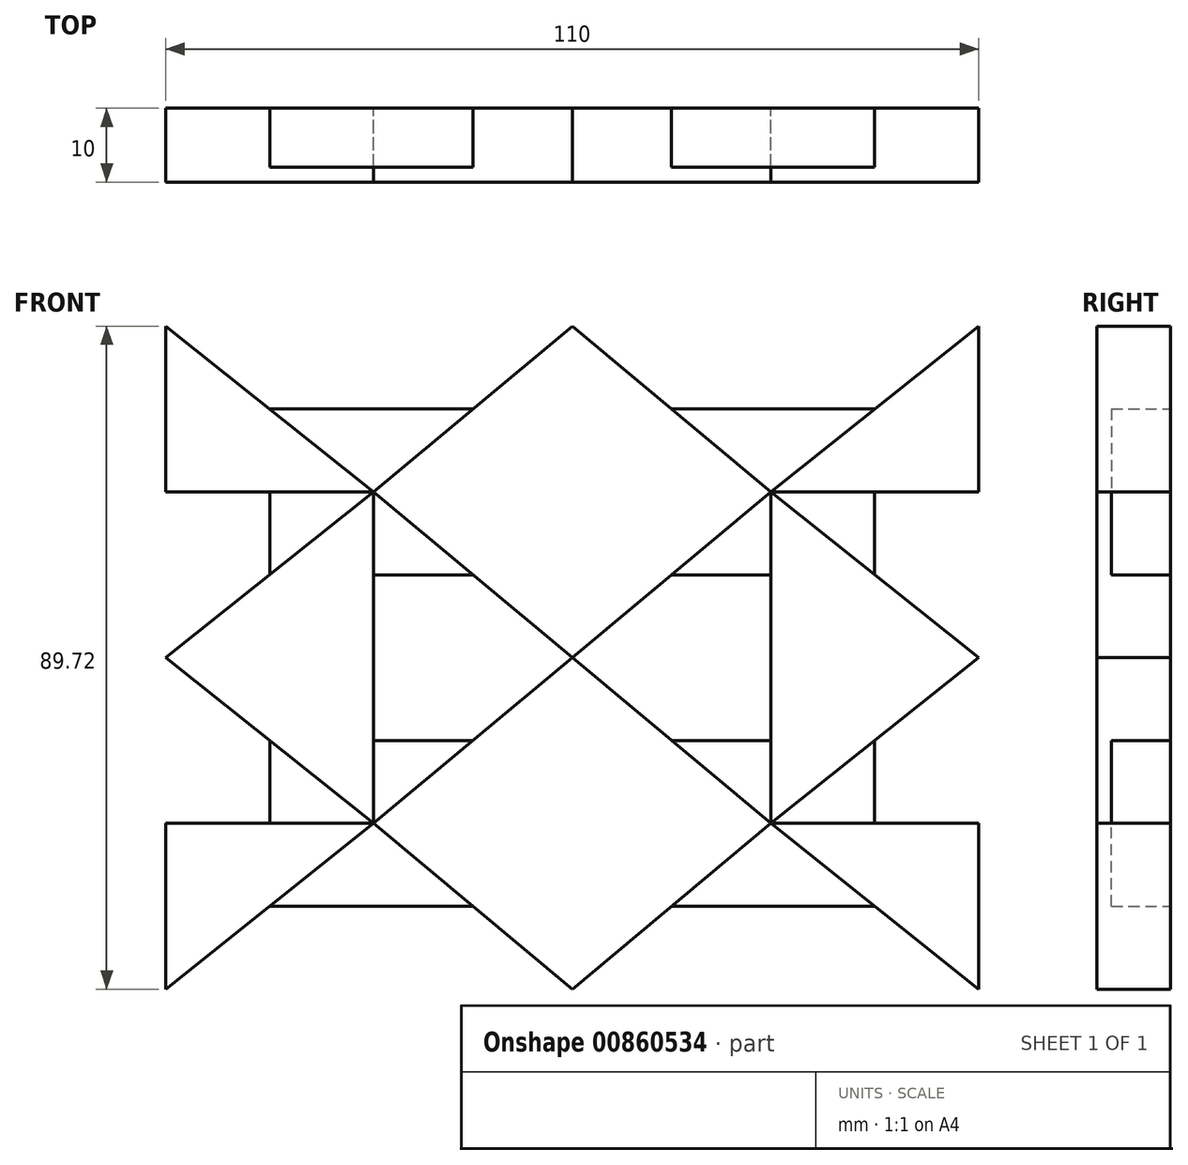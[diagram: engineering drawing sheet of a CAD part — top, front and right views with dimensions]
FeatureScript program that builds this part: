
annotation { "Feature Type Name" : "Feature", "Feature Type Description" : "" }
export const myFeature = defineFeature(function(context is Context, id is Id, definition is map)
    precondition{}
    {
        {
            var Q0;
            Q0=qCreatedBy(makeId("Front.planeOp"),FACE);
            var sketch = newSketch(context, id + "F0", { "sketchPlane" : qUnion([Q0])});
            skLineSegment(sketch, "E0", {"start": v(0, 0) * mm, "end": v(-26.87, 22.43) * mm});
            skLineSegment(sketch, "E1", {"start": v(-26.87, 22.43) * mm, "end": v(-55, 0) * mm});
            skLineSegment(sketch, "E2", {"start": v(0, 0) * mm, "end": v(26.87, 22.43) * mm});
            skLineSegment(sketch, "E3", {"start": v(26.87, 22.43) * mm, "end": v(55, 0) * mm});
            skLineSegment(sketch, "E4", {"start": v(0, 0) * mm, "end": v(-55, 0) * mm});
            skLineSegment(sketch, "E5", {"start": v(0, 0) * mm, "end": v(55, 0) * mm});
            skLineSegment(sketch, "E6", {"start": v(-26.87, 22.43) * mm, "end": v(-26.87, 0) * mm});
            skLineSegment(sketch, "E7", {"start": v(26.87, 22.43) * mm, "end": v(26.87, 0) * mm});
            skLineSegment(sketch, "E8", {"start": v(-26.87, 0) * mm, "end": v(-26.87, -22.43) * mm});
            skLineSegment(sketch, "E9", {"start": v(-55, 0) * mm, "end": v(-26.87, -22.43) * mm});
            skLineSegment(sketch, "E10", {"start": v(-26.87, -22.43) * mm, "end": v(0, 0) * mm});
            skLineSegment(sketch, "E11", {"start": v(26.87, 0) * mm, "end": v(26.87, -22.43) * mm});
            skLineSegment(sketch, "E12", {"start": v(0, 0) * mm, "end": v(26.87, -22.43) * mm});
            skLineSegment(sketch, "E13", {"start": v(26.87, -22.43) * mm, "end": v(55, 0) * mm});
            skLineSegment(sketch, "E14", {"start": v(0, 0) * mm, "end": v(0, 44.86) * mm});
            skLineSegment(sketch, "E15", {"start": v(0, 44.86) * mm, "end": v(-26.87, 22.43) * mm});
            skLineSegment(sketch, "E16", {"start": v(0, 44.86) * mm, "end": v(26.87, 22.43) * mm});
            skLineSegment(sketch, "E17", {"start": v(-55, 0) * mm, "end": v(-55, 22.43) * mm});
            skLineSegment(sketch, "E18", {"start": v(-55, 22.43) * mm, "end": v(-26.87, 22.43) * mm});
            skLineSegment(sketch, "E19", {"start": v(-55, 22.43) * mm, "end": v(-55, 44.86) * mm});
            skLineSegment(sketch, "E20", {"start": v(-55, 44.86) * mm, "end": v(0, 44.86) * mm});
            skLineSegment(sketch, "E21", {"start": v(-55, 44.86) * mm, "end": v(-26.87, 22.43) * mm});
            skLineSegment(sketch, "E22", {"start": v(55, 0) * mm, "end": v(55, 22.43) * mm});
            skLineSegment(sketch, "E23", {"start": v(55, 22.43) * mm, "end": v(26.87, 22.43) * mm});
            skLineSegment(sketch, "E24", {"start": v(55, 22.43) * mm, "end": v(55, 44.86) * mm});
            skLineSegment(sketch, "E25", {"start": v(55, 44.86) * mm, "end": v(0, 44.86) * mm});
            skLineSegment(sketch, "E26", {"start": v(0, 0) * mm, "end": v(0, -44.86) * mm});
            skLineSegment(sketch, "E27", {"start": v(0, -44.86) * mm, "end": v(-26.87, -22.43) * mm});
            skLineSegment(sketch, "E28", {"start": v(0, -44.86) * mm, "end": v(26.87, -22.43) * mm});
            skLineSegment(sketch, "E29", {"start": v(-55, 0) * mm, "end": v(-55, -22.43) * mm});
            skLineSegment(sketch, "E30", {"start": v(-55, -22.43) * mm, "end": v(-26.87, -22.43) * mm});
            skLineSegment(sketch, "E31", {"start": v(-55, -22.43) * mm, "end": v(-55, -44.86) * mm});
            skLineSegment(sketch, "E32", {"start": v(-55, -44.86) * mm, "end": v(0, -44.86) * mm});
            skLineSegment(sketch, "E33", {"start": v(-26.87, -22.43) * mm, "end": v(-55, -44.86) * mm});
            skLineSegment(sketch, "E34", {"start": v(0, -44.86) * mm, "end": v(55, -44.86) * mm});
            skLineSegment(sketch, "E35", {"start": v(55, 0) * mm, "end": v(55, -22.43) * mm});
            skLineSegment(sketch, "E36", {"start": v(55, -22.43) * mm, "end": v(26.87, -22.43) * mm});
            skLineSegment(sketch, "E37", {"start": v(55, -22.43) * mm, "end": v(55, -44.86) * mm});
            skLineSegment(sketch, "E38", {"start": v(26.87, -22.43) * mm, "end": v(55, -44.86) * mm});
            skLineSegment(sketch, "E39", {"start": v(26.87, 22.43) * mm, "end": v(55, 44.86) * mm});
            skLineSegment(sketch, "E40", {"start": v(-26.87, -11.21) * mm, "end": v(-13.44, -11.21) * mm});
            skLineSegment(sketch, "E41", {"start": v(-40.94, -11.21) * mm, "end": v(-40.94, -22.43) * mm});
            skLineSegment(sketch, "E42", {"start": v(-40.94, -33.64) * mm, "end": v(-13.44, -33.64) * mm});
            skLineSegment(sketch, "E43", {"start": v(13.44, -33.64) * mm, "end": v(40.94, -33.64) * mm});
            skLineSegment(sketch, "E44", {"start": v(40.94, -11.21) * mm, "end": v(40.94, -22.43) * mm});
            skLineSegment(sketch, "E45", {"start": v(13.44, -11.22) * mm, "end": v(26.87, -11.21) * mm});
            skLineSegment(sketch, "E46", {"start": v(-26.87, 11.21) * mm, "end": v(-13.44, 11.21) * mm});
            skLineSegment(sketch, "E47", {"start": v(13.44, 11.21) * mm, "end": v(26.87, 11.21) * mm});
            skLineSegment(sketch, "E48", {"start": v(13.44, 33.64) * mm, "end": v(40.94, 33.64) * mm});
            skLineSegment(sketch, "E49", {"start": v(40.94, 22.43) * mm, "end": v(40.94, 11.21) * mm});
            skLineSegment(sketch, "E50", {"start": v(-13.44, 33.64) * mm, "end": v(-40.94, 33.64) * mm});
            skLineSegment(sketch, "E51", {"start": v(-40.94, 22.43) * mm, "end": v(-40.94, 11.21) * mm});
            skSolve(sketch);
        }
        {
            var Q0;
            {var subQ1=sQuery(id+"F0.wireOp",EDGE,"E19");Q0=makeQuery(id+"F0.imprint","IMPRINT",FACE,{"disambiguationData":[TD([[makeQuery(id+"F0.imprint","IMPRINT",EDGE,{"derivedFrom":subQ1}),-1.0]])]});}
            var Q1;
            {var subQ5=sQuery(id+"F0.wireOp",EDGE,"E24");Q1=makeQuery(id+"F0.imprint","IMPRINT",FACE,{"disambiguationData":[TD([[makeQuery(id+"F0.imprint","IMPRINT",EDGE,{"derivedFrom":subQ5}),1.0]])]});}
            var Q2;
            {var subQ4=sQuery(id+"F0.wireOp",EDGE,"E31");Q2=makeQuery(id+"F0.imprint","IMPRINT",FACE,{"disambiguationData":[TD([[makeQuery(id+"F0.imprint","IMPRINT",EDGE,{"derivedFrom":subQ4}),1.0]])]});}
            var Q3;
            {var subQ4=sQuery(id+"F0.wireOp",EDGE,"E37");Q3=makeQuery(id+"F0.imprint","IMPRINT",FACE,{"disambiguationData":[TD([[makeQuery(id+"F0.imprint","IMPRINT",EDGE,{"derivedFrom":subQ4}),-1.0]])]});}
            var Q4;
            {var subQ1=sQuery(id+"F0.wireOp",EDGE,"E14");Q4=makeQuery(id+"F0.imprint","IMPRINT",FACE,{"disambiguationData":[TD([[makeQuery(id+"F0.imprint","IMPRINT",EDGE,{"derivedFrom":subQ1}),1.0]])]});}
            var Q5;
            {var subQ3=sQuery(id+"F0.wireOp",EDGE,"E6");var subQ7=makeQuery(id+"F0.imprint","INTERSECT",VERTEX,{"derivedFrom":[subQ3,sQuery(id+"F0.wireOp",EDGE,"E46")]});Q5=makeQuery(id+"F0.imprint","IMPRINT",FACE,{"disambiguationData":[TD([[makeQuery(id+"F0.imprint","IMPRINT",EDGE,{"disambiguationData":[TD([[subQ7,-1.0]])],"derivedFrom":subQ3}),-1.0]])]});}
            var Q6;
            {var subQ1=sQuery(id+"F0.wireOp",EDGE,"E14");Q6=makeQuery(id+"F0.imprint","IMPRINT",FACE,{"disambiguationData":[TD([[makeQuery(id+"F0.imprint","IMPRINT",EDGE,{"derivedFrom":subQ1}),-1.0]])]});}
            var Q7;
            {var subQ4=sQuery(id+"F0.wireOp",EDGE,"E8");var subQ6=makeQuery(id+"F0.imprint","INTERSECT",VERTEX,{"derivedFrom":[subQ4,sQuery(id+"F0.wireOp",EDGE,"E40")]});Q7=makeQuery(id+"F0.imprint","IMPRINT",FACE,{"disambiguationData":[TD([[makeQuery(id+"F0.imprint","IMPRINT",EDGE,{"disambiguationData":[TD([[subQ6,1.0]])],"derivedFrom":subQ4}),-1.0]])]});}
            var Q8;
            {var subQ1=sQuery(id+"F0.wireOp",EDGE,"E11");var subQ3=makeQuery(id+"F0.imprint","INTERSECT",VERTEX,{"derivedFrom":[subQ1,sQuery(id+"F0.wireOp",EDGE,"E45")]});Q8=makeQuery(id+"F0.imprint","IMPRINT",FACE,{"disambiguationData":[TD([[makeQuery(id+"F0.imprint","IMPRINT",EDGE,{"disambiguationData":[TD([[subQ3,1.0]])],"derivedFrom":subQ1}),1.0]])]});}
            var Q9;
            {var subQ1=sQuery(id+"F0.wireOp",EDGE,"E26");Q9=makeQuery(id+"F0.imprint","IMPRINT",FACE,{"disambiguationData":[TD([[makeQuery(id+"F0.imprint","IMPRINT",EDGE,{"derivedFrom":subQ1}),-1.0]])]});}
            var Q10;
            {var subQ1=sQuery(id+"F0.wireOp",EDGE,"E26");Q10=makeQuery(id+"F0.imprint","IMPRINT",FACE,{"disambiguationData":[TD([[makeQuery(id+"F0.imprint","IMPRINT",EDGE,{"derivedFrom":subQ1}),1.0]])]});}
            var Q11;
            {var subQ0=sQuery(id+"F0.wireOp",EDGE,"E7");var subQ3=makeQuery(id+"F0.imprint","INTERSECT",VERTEX,{"derivedFrom":[subQ0,sQuery(id+"F0.wireOp",EDGE,"E47")]});Q11=makeQuery(id+"F0.imprint","IMPRINT",FACE,{"disambiguationData":[TD([[makeQuery(id+"F0.imprint","IMPRINT",EDGE,{"disambiguationData":[TD([[subQ3,-1.0]])],"derivedFrom":subQ0}),1.0]])]});}
            extrude(context, id + "F1", {"entities" : qUnion([Q0, Q1, Q2, Q3, Q4, Q5, Q6, Q7, Q8, Q9, Q10, Q11]), "depth" : 10 * mm, "offsetDistance" : 25 * mm, "hasSecondDirection" : true, "secondDirectionOppositeDirection" : true, "secondDirectionDepth" : 0 * mm});
        }
        {
            var Q0;
            {var subQ3=sQuery(id+"F0.wireOp",EDGE,"E50");Q0=makeQuery(id+"F0.imprint","IMPRINT",FACE,{"disambiguationData":[TD([[makeQuery(id+"F0.imprint","IMPRINT",EDGE,{"derivedFrom":subQ3}),1.0]])]});}
            var Q1;
            {var subQ3=sQuery(id+"F0.wireOp",EDGE,"E51");Q1=makeQuery(id+"F0.imprint","IMPRINT",FACE,{"disambiguationData":[TD([[makeQuery(id+"F0.imprint","IMPRINT",EDGE,{"derivedFrom":subQ3}),1.0]])]});}
            var Q2;
            {var subQ3=sQuery(id+"F0.wireOp",EDGE,"E46");Q2=makeQuery(id+"F0.imprint","IMPRINT",FACE,{"disambiguationData":[TD([[makeQuery(id+"F0.imprint","IMPRINT",EDGE,{"derivedFrom":subQ3}),1.0]])]});}
            var Q3;
            {var subQ3=sQuery(id+"F0.wireOp",EDGE,"E41");Q3=makeQuery(id+"F0.imprint","IMPRINT",FACE,{"disambiguationData":[TD([[makeQuery(id+"F0.imprint","IMPRINT",EDGE,{"derivedFrom":subQ3}),1.0]])]});}
            var Q4;
            {var subQ3=sQuery(id+"F0.wireOp",EDGE,"E40");Q4=makeQuery(id+"F0.imprint","IMPRINT",FACE,{"disambiguationData":[TD([[makeQuery(id+"F0.imprint","IMPRINT",EDGE,{"derivedFrom":subQ3}),-1.0]])]});}
            var Q5;
            {var subQ3=sQuery(id+"F0.wireOp",EDGE,"E42");Q5=makeQuery(id+"F0.imprint","IMPRINT",FACE,{"disambiguationData":[TD([[makeQuery(id+"F0.imprint","IMPRINT",EDGE,{"derivedFrom":subQ3}),1.0]])]});}
            var Q6;
            {var subQ3=sQuery(id+"F0.wireOp",EDGE,"E45");Q6=makeQuery(id+"F0.imprint","IMPRINT",FACE,{"disambiguationData":[TD([[makeQuery(id+"F0.imprint","IMPRINT",EDGE,{"derivedFrom":subQ3}),-1.0]])]});}
            var Q7;
            {var subQ3=sQuery(id+"F0.wireOp",EDGE,"E44");Q7=makeQuery(id+"F0.imprint","IMPRINT",FACE,{"disambiguationData":[TD([[makeQuery(id+"F0.imprint","IMPRINT",EDGE,{"derivedFrom":subQ3}),-1.0]])]});}
            var Q8;
            {var subQ3=sQuery(id+"F0.wireOp",EDGE,"E48");Q8=makeQuery(id+"F0.imprint","IMPRINT",FACE,{"disambiguationData":[TD([[makeQuery(id+"F0.imprint","IMPRINT",EDGE,{"derivedFrom":subQ3}),-1.0]])]});}
            var Q9;
            {var subQ3=sQuery(id+"F0.wireOp",EDGE,"E47");Q9=makeQuery(id+"F0.imprint","IMPRINT",FACE,{"disambiguationData":[TD([[makeQuery(id+"F0.imprint","IMPRINT",EDGE,{"derivedFrom":subQ3}),1.0]])]});}
            var Q10;
            {var subQ3=sQuery(id+"F0.wireOp",EDGE,"E49");Q10=makeQuery(id+"F0.imprint","IMPRINT",FACE,{"disambiguationData":[TD([[makeQuery(id+"F0.imprint","IMPRINT",EDGE,{"derivedFrom":subQ3}),-1.0]])]});}
            var Q11;
            {var subQ3=sQuery(id+"F0.wireOp",EDGE,"E43");Q11=makeQuery(id+"F0.imprint","IMPRINT",FACE,{"disambiguationData":[TD([[makeQuery(id+"F0.imprint","IMPRINT",EDGE,{"derivedFrom":subQ3}),1.0]])]});}
            extrude(context, id + "F2", {"entities" : qUnion([Q0, Q1, Q2, Q3, Q4, Q5, Q6, Q7, Q8, Q9, Q10, Q11]), "depth" : 8 * mm, "offsetDistance" : 25 * mm});
        }
    });
